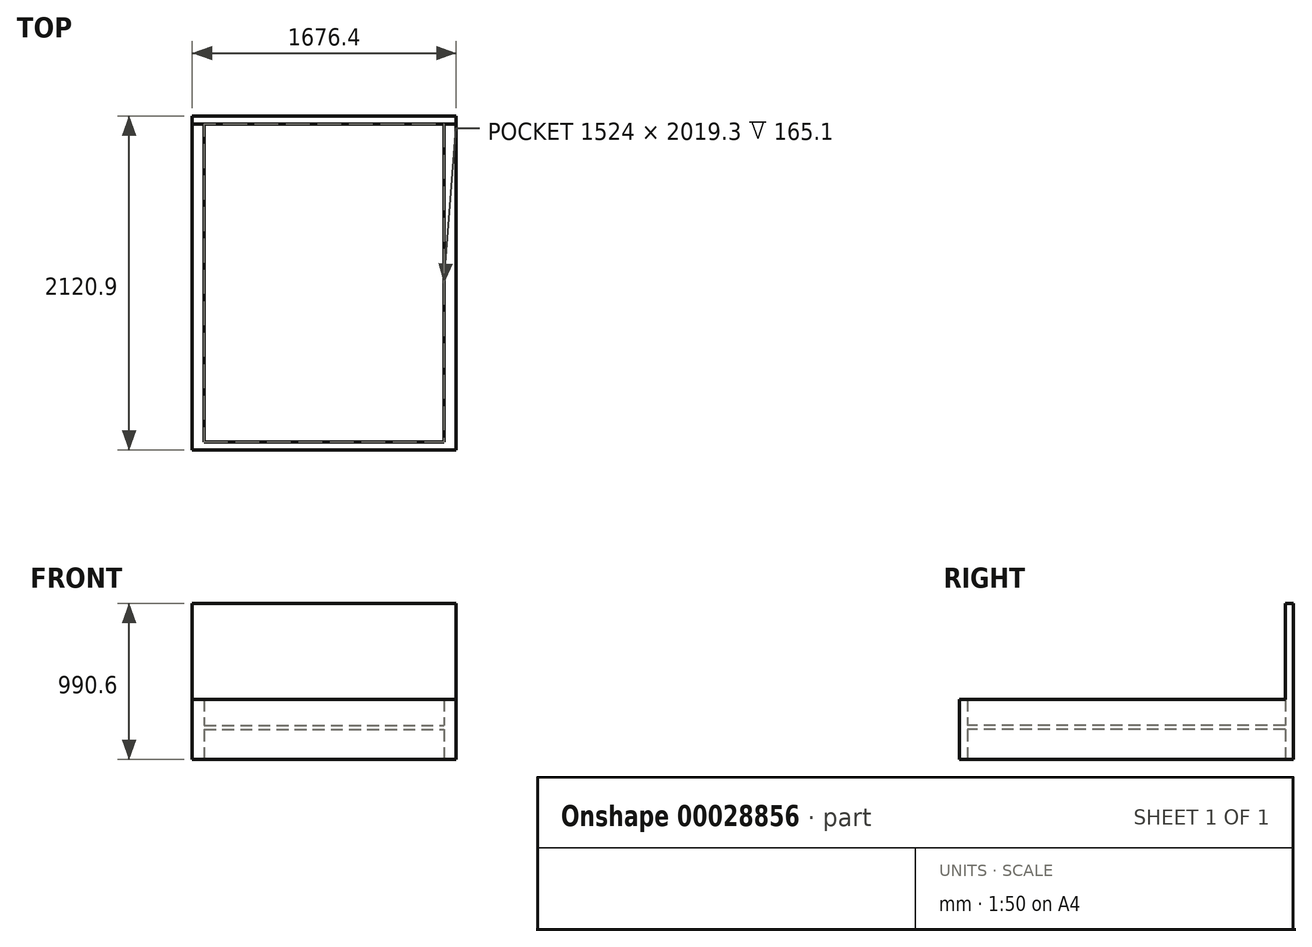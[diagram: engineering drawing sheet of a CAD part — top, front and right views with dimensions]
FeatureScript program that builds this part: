
annotation { "Feature Type Name" : "Feature", "Feature Type Description" : "" }
export const myFeature = defineFeature(function(context is Context, id is Id, definition is map)
    precondition{}
    {
        {
            var Q0;
            Q0=qCreatedBy(makeId("Top.planeOp"),FACE);
            var sketch = newSketch(context, id + "F0", { "sketchPlane" : qUnion([Q0])});
            skLineSegment(sketch, "E0.bottom", {"start": v(-762, 1009.65) * mm, "end": v(762, 1009.65) * mm});
            skLineSegment(sketch, "E0.top", {"start": v(-762, -1009.65) * mm, "end": v(762, -1009.65) * mm});
            skLineSegment(sketch, "E0.left", {"start": v(-762, 1009.65) * mm, "end": v(-762, -1009.65) * mm});
            skLineSegment(sketch, "E0.right", {"start": v(762, 1009.65) * mm, "end": v(762, -1009.65) * mm});
            skPoint(sketch, "E0.middle", {"position": v(0, 0) * mm});
            skLineSegment(sketch, "E1.bottom", {"start": v(-838.2, 1060.45) * mm, "end": v(838.2, 1060.45) * mm});
            skLineSegment(sketch, "E1.top", {"start": v(-838.2, -1060.45) * mm, "end": v(838.2, -1060.45) * mm});
            skLineSegment(sketch, "E1.left", {"start": v(-838.2, 1060.45) * mm, "end": v(-838.2, -1060.45) * mm});
            skLineSegment(sketch, "E1.right", {"start": v(838.2, 1060.45) * mm, "end": v(838.2, -1060.45) * mm});
            skSolve(sketch);
        }
        {
            var Q0;
            Q0=makeQuery(id+"F0.imprint","IMPRINT",FACE,{"disambiguationData":[TD([[makeQuery(id+"F0.imprint","IMPRINT",EDGE,{"derivedFrom":sQuery(id+"F0.wireOp",EDGE,"E0.bottom")}),1.0]])]});
            extrude(context, id + "F1", {"entities" : qUnion([Q0]), "depth" : 190.5 * mm, "hasSecondDirection" : true, "secondDirectionOppositeDirection" : true, "secondDirectionDepth" : 190.5 * mm});
        }
        {
            var Q0;
            Q0=qCreatedBy(makeId("Top.planeOp"),FACE);
            var sketch = newSketch(context, id + "F2", { "sketchPlane" : qUnion([Q0])});
            skLineSegment(sketch, "E2.bottom", {"start": v(-762, 1009.65) * mm, "end": v(762, 1009.65) * mm});
            skLineSegment(sketch, "E2.top", {"start": v(-762, -1009.65) * mm, "end": v(762, -1009.65) * mm});
            skLineSegment(sketch, "E2.left", {"start": v(-762, 1009.65) * mm, "end": v(-762, -1009.65) * mm});
            skLineSegment(sketch, "E2.right", {"start": v(762, 1009.65) * mm, "end": v(762, -1009.65) * mm});
            skPoint(sketch, "E2.middle", {"position": v(0, 0) * mm});
            skSolve(sketch);
        }
        {
            var Q0;
            Q0=makeQuery(id+"F2.imprint","IMPRINT",FACE,{"disambiguationData":[TD([[makeQuery(id+"F2.imprint","IMPRINT",EDGE,{"derivedFrom":sQuery(id+"F2.wireOp",EDGE,"E2.bottom")}),-1.0]])]});
            extrude(context, id + "F3", {"entities" : qUnion([Q0]), "operationType" : NewBodyOperationType.ADD, "depth" : 25.4 * mm});
        }
        {
            var Q0;
            Q0=makeQuery(id+"F1.opExtrude","CAP_FACE",FACE,{"disambiguationData":[OSD([sQuery(id+"F0.wireOp",EDGE,"E0.bottom"),sQuery(id+"F0.wireOp",EDGE,"E0.top"),sQuery(id+"F0.wireOp",EDGE,"E0.left"),sQuery(id+"F0.wireOp",EDGE,"E0.right"),sQuery(id+"F0.wireOp",EDGE,"E1.bottom"),sQuery(id+"F0.wireOp",EDGE,"E1.top"),sQuery(id+"F0.wireOp",EDGE,"E1.left"),sQuery(id+"F0.wireOp",EDGE,"E1.right")])],"isStart":false});
            var sketch = newSketch(context, id + "F4", { "sketchPlane" : qUnion([Q0])});
            skLineSegment(sketch, "E3.bottom", {"start": v(-838.2, 1060.45) * mm, "end": v(838.2, 1060.45) * mm});
            skLineSegment(sketch, "E3.top", {"start": v(-838.2, 1009.65) * mm, "end": v(838.2, 1009.65) * mm});
            skLineSegment(sketch, "E3.left", {"start": v(-838.2, 1060.45) * mm, "end": v(-838.2, 1009.65) * mm});
            skLineSegment(sketch, "E3.right", {"start": v(838.2, 1060.45) * mm, "end": v(838.2, 1009.65) * mm});
            skSolve(sketch);
        }
        {
            var Q0;
            Q0=qSketchRegion(id+"F4",true);
            extrude(context, id + "F5", {"entities" : qUnion([Q0]), "operationType" : NewBodyOperationType.ADD, "depth" : 609.6 * mm});
        }
    });
